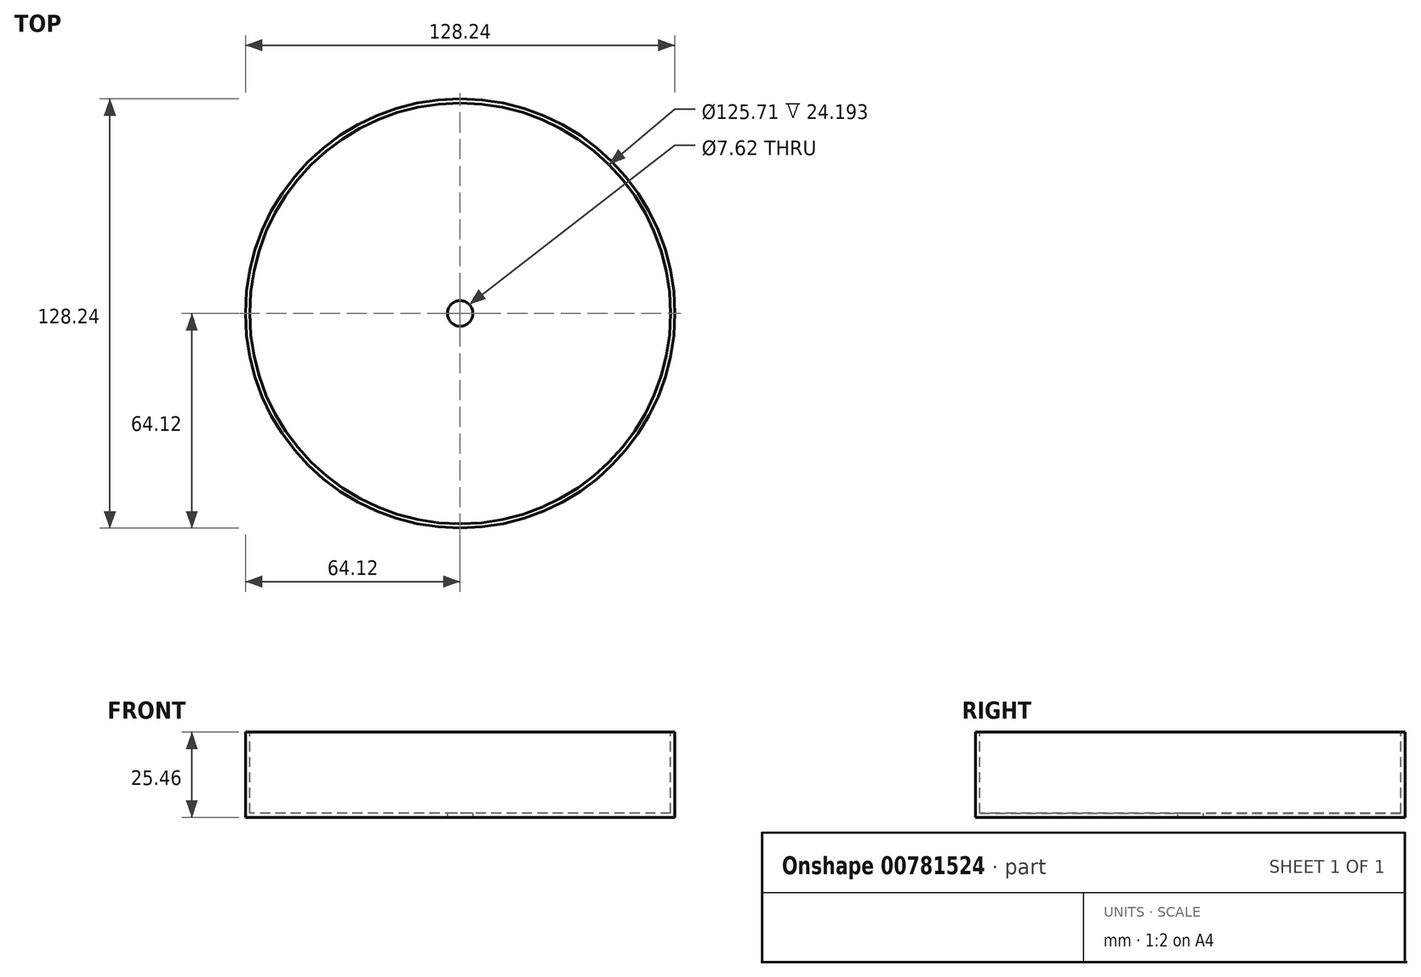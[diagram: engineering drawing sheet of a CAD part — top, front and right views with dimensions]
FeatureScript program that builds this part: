
annotation { "Feature Type Name" : "Feature", "Feature Type Description" : "" }
export const myFeature = defineFeature(function(context is Context, id is Id, definition is map)
    precondition{}
    {
        {
            var Q0;
            Q0=qCreatedBy(makeId("Front.planeOp"),FACE);
            var sketch = newSketch(context, id + "F0", { "sketchPlane" : qUnion([Q0])});
            skLineSegment(sketch, "E0.bottom", {"start": v(0, 0) * mm, "end": v(64.12, 0) * mm});
            skLineSegment(sketch, "E0.top", {"start": v(0, 25.46) * mm, "end": v(64.12, 25.46) * mm});
            skLineSegment(sketch, "E0.left", {"start": v(0, 0) * mm, "end": v(0, 25.46) * mm});
            skLineSegment(sketch, "E0.right", {"start": v(64.12, 0) * mm, "end": v(64.12, 25.46) * mm});
            skLineSegment(sketch, "E1", {"start": v(0, 75.22) * mm, "end": v(0, -65.18) * mm, "construction": true});
            skSolve(sketch);
        }
        {
            var Q0;
            Q0 = qSketchRegion(id + "F0", true);
            var Q1;
            Q1=sQuery(id+"F0.wireOp",EDGE,"E1");
            revolve(context, id + "F1", {"surfaceOperationType" : NewSurfaceOperationType.NEW, "entities" : qUnion([Q0]), "axis" : qUnion([Q1]), "revolveType" : RevolveType.FULL});
        }
        {
            var Q0;
            Q0=makeQuery(id+"F1.opRevolve","SWEPT_FACE",FACE,{"disambiguationData":[OSD([sQuery(id+"F0.wireOp",EDGE,"E0.top")])]});
            shell(context, id + "F2", {"entities" : qUnion([Q0]), "thickness" : 1.27 * mm});
        }
        {
            var Q0;
            Q0=qCreatedBy(makeId("Top.planeOp"),FACE);
            var sketch = newSketch(context, id + "F3", { "sketchPlane" : qUnion([Q0])});
            skPoint(sketch, "E2", {"position": v(0, 0) * mm});
            skSolve(sketch);
        }
        {
            var Q0;
            Q0=sQuery(id+"F3.wireOp",VERTEX,"E2");
            var Q1;
            Q1=makeQuery(id+"F1.opRevolve","SWEPT_BODY",BODY,{"disambiguationData":[OSD([sQuery(id+"F0.wireOp",EDGE,"E0.bottom"),sQuery(id+"F0.wireOp",EDGE,"E0.top"),sQuery(id+"F0.wireOp",EDGE,"E0.left"),sQuery(id+"F0.wireOp",EDGE,"E0.right")])]});
            hole(context, id + "F4", {"style" : HoleStyle.SIMPLE, "endStyle" : HoleEndStyle.THROUGH, "oppositeDirection" : true, "holeDiameter" : 7.62 * mm, "majorDiameter" : 6.35 * mm, "isTappedThrough" : true, "tappedDepth" : 12.7 * mm, "tapClearance" : 3, "locations" : qUnion([Q0]), "scope" : qUnion([Q1])});
        }
    });
